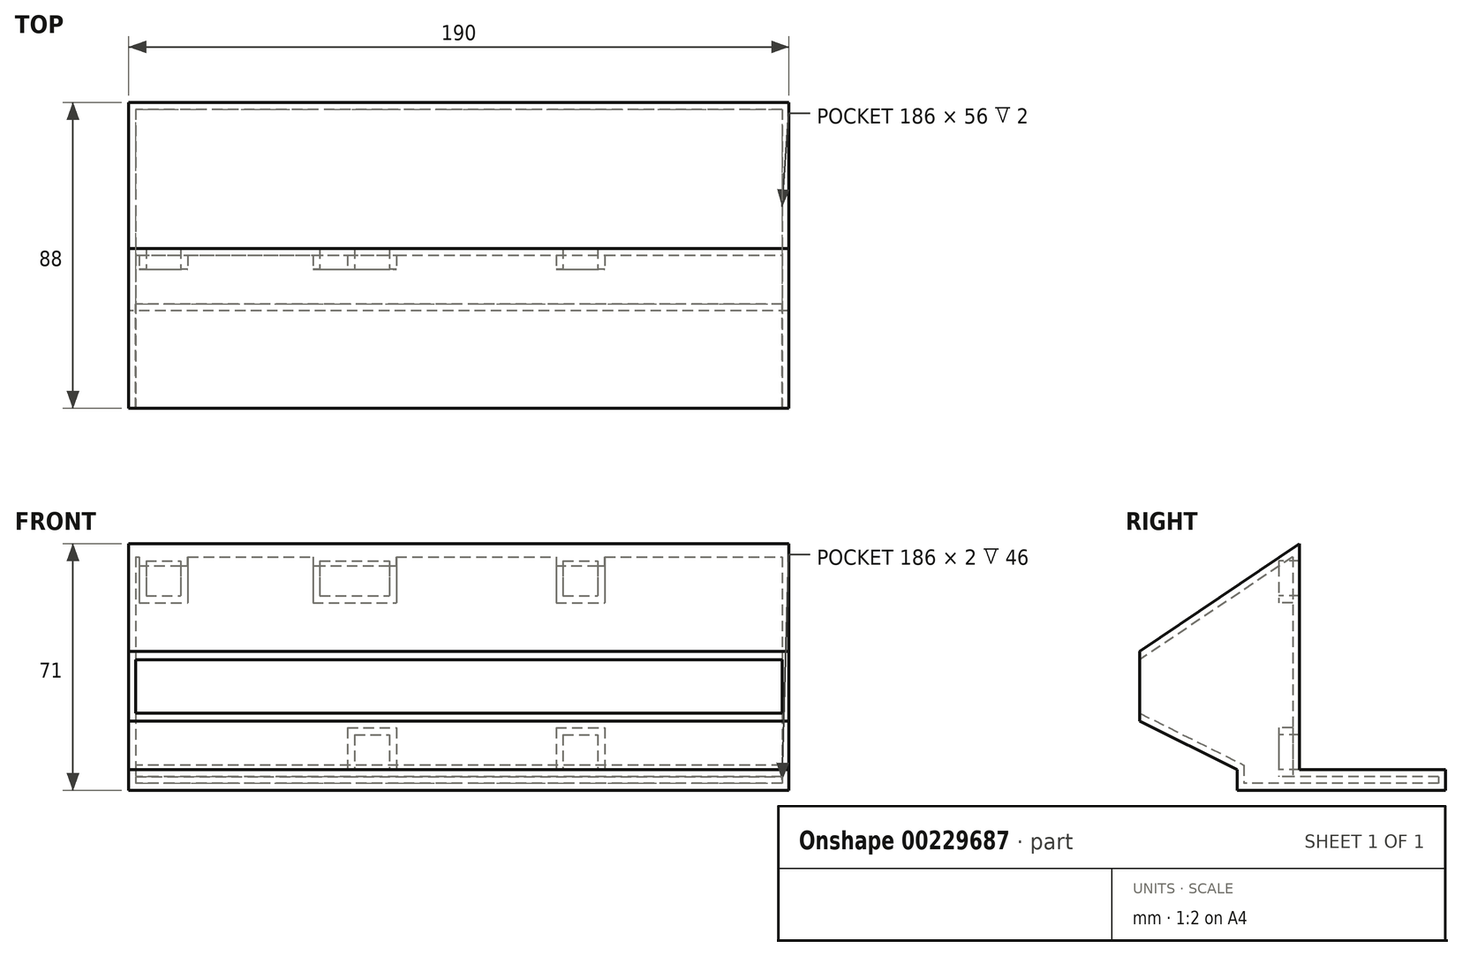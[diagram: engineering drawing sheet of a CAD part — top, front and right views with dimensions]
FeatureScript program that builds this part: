
annotation { "Feature Type Name" : "Feature", "Feature Type Description" : "" }
export const myFeature = defineFeature(function(context is Context, id is Id, definition is map)
    precondition{}
    {
        {
            var Q0;
            Q0=qCreatedBy(makeId("Top.planeOp"),FACE);
            var sketch = newSketch(context, id + "F0", { "sketchPlane" : qUnion([Q0])});
            skLineSegment(sketch, "E0.bottom", {"start": v(95, 30) * mm, "end": v(-95, 30) * mm});
            skLineSegment(sketch, "E0.top", {"start": v(95, -30) * mm, "end": v(-95, -30) * mm});
            skLineSegment(sketch, "E0.left", {"start": v(95, 30) * mm, "end": v(95, -30) * mm});
            skLineSegment(sketch, "E0.right", {"start": v(-95, 30) * mm, "end": v(-95, -30) * mm});
            skPoint(sketch, "E0.middle", {"position": v(0, 0) * mm});
            skSolve(sketch);
        }
        {
            var Q0;
            Q0=makeQuery(id+"F0.imprint","IMPRINT",FACE,{"disambiguationData":[TD([[makeQuery(id+"F0.imprint","IMPRINT",EDGE,{"derivedFrom":sQuery(id+"F0.wireOp",EDGE,"E0.bottom")}),1.0]])]});
            extrude(context, id + "F1", {"entities" : qUnion([Q0]), "depth" : 6 * mm});
        }
        {
            var Q0;
            Q0=makeQuery(id+"F1.opExtrude","CAP_FACE",FACE,{"disambiguationData":[OSD([sQuery(id+"F0.wireOp",EDGE,"E0.bottom"),sQuery(id+"F0.wireOp",EDGE,"E0.top"),sQuery(id+"F0.wireOp",EDGE,"E0.left"),sQuery(id+"F0.wireOp",EDGE,"E0.right")])],"isStart":false});
            var sketch = newSketch(context, id + "F2", { "sketchPlane" : qUnion([Q0])});
            skLineSegment(sketch, "E1.bottom", {"start": v(-95, -12) * mm, "end": v(95, -12) * mm});
            skLineSegment(sketch, "E1.top", {"start": v(-95, -18) * mm, "end": v(95, -18) * mm});
            skLineSegment(sketch, "E1.left", {"start": v(-95, -12) * mm, "end": v(-95, -18) * mm});
            skLineSegment(sketch, "E1.right", {"start": v(95, -12) * mm, "end": v(95, -18) * mm});
            skSolve(sketch);
        }
        {
            var Q0;
            Q0=makeQuery(id+"F2.imprint","IMPRINT",FACE,{"disambiguationData":[TD([[makeQuery(id+"F2.imprint","IMPRINT",EDGE,{"derivedFrom":sQuery(id+"F2.wireOp",EDGE,"E1.bottom")}),-1.0]])]});
            extrude(context, id + "F3", {"entities" : qUnion([Q0]), "operationType" : NewBodyOperationType.ADD, "depth" : 65 * mm});
        }
        {
            var Q0;
            Q0=makeQuery(id+"F3.opExtrude","SWEPT_FACE",FACE,{"disambiguationData":[OSD([sQuery(id+"F2.wireOp",EDGE,"E1.top")])]});
            var sketch = newSketch(context, id + "F4", { "sketchPlane" : qUnion([Q0])});
            skLineSegment(sketch, "E2.bottom", {"start": v(-90, 66) * mm, "end": v(-30, 66) * mm});
            skLineSegment(sketch, "E2.top", {"start": v(-90, 6) * mm, "end": v(-30, 6) * mm});
            skLineSegment(sketch, "E2.left", {"start": v(-90, 66) * mm, "end": v(-90, 6) * mm});
            skLineSegment(sketch, "E2.right", {"start": v(-30, 66) * mm, "end": v(-30, 6) * mm});
            skLineSegment(sketch, "E3.MirrorCS", {"start": v(30, 66) * mm, "end": v(-30, 66) * mm});
            skLineSegment(sketch, "E4.MirrorCS", {"start": v(30, 66) * mm, "end": v(30, 6) * mm});
            skLineSegment(sketch, "E5.MirrorCS", {"start": v(30, 6) * mm, "end": v(-30, 6) * mm});
            skLineSegment(sketch, "E6.MirrorCS", {"start": v(30, 66) * mm, "end": v(90, 66) * mm});
            skLineSegment(sketch, "E7.MirrorCS", {"start": v(90, 66) * mm, "end": v(90, 6) * mm});
            skLineSegment(sketch, "E8.MirrorCS", {"start": v(30, 6) * mm, "end": v(90, 6) * mm});
            skLineSegment(sketch, "E9.bottom", {"start": v(-90, 66) * mm, "end": v(-80, 66) * mm});
            skLineSegment(sketch, "E9.top", {"start": v(-90, 56) * mm, "end": v(-80, 56) * mm});
            skLineSegment(sketch, "E9.left", {"start": v(-90, 66) * mm, "end": v(-90, 56) * mm});
            skLineSegment(sketch, "E9.right", {"start": v(-80, 66) * mm, "end": v(-80, 56) * mm});
            skLineSegment(sketch, "E10.bottom", {"start": v(-90, 16) * mm, "end": v(-80, 16) * mm});
            skLineSegment(sketch, "E10.top", {"start": v(-90, 6) * mm, "end": v(-80, 6) * mm});
            skLineSegment(sketch, "E10.left", {"start": v(-90, 16) * mm, "end": v(-90, 6) * mm});
            skLineSegment(sketch, "E10.right", {"start": v(-80, 16) * mm, "end": v(-80, 6) * mm});
            skLineSegment(sketch, "E11.bottom", {"start": v(-40, 66) * mm, "end": v(-30, 66) * mm});
            skLineSegment(sketch, "E11.top", {"start": v(-40, 56) * mm, "end": v(-30, 56) * mm});
            skLineSegment(sketch, "E11.left", {"start": v(-40, 66) * mm, "end": v(-40, 56) * mm});
            skLineSegment(sketch, "E11.right", {"start": v(-30, 66) * mm, "end": v(-30, 56) * mm});
            skLineSegment(sketch, "E12.bottom", {"start": v(-40, 16) * mm, "end": v(-30, 16) * mm});
            skLineSegment(sketch, "E12.top", {"start": v(-40, 6) * mm, "end": v(-30, 6) * mm});
            skLineSegment(sketch, "E12.left", {"start": v(-40, 16) * mm, "end": v(-40, 6) * mm});
            skLineSegment(sketch, "E12.right", {"start": v(-30, 16) * mm, "end": v(-30, 6) * mm});
            skLineSegment(sketch, "E13.bottom", {"start": v(-30, 66) * mm, "end": v(-20, 66) * mm});
            skLineSegment(sketch, "E13.top", {"start": v(-30, 56) * mm, "end": v(-20, 56) * mm});
            skLineSegment(sketch, "E13.right", {"start": v(-20, 66) * mm, "end": v(-20, 56) * mm});
            skLineSegment(sketch, "E14.bottom", {"start": v(-30, 16) * mm, "end": v(-20, 16) * mm});
            skLineSegment(sketch, "E14.top", {"start": v(-30, 6) * mm, "end": v(-20, 6) * mm});
            skLineSegment(sketch, "E14.right", {"start": v(-20, 16) * mm, "end": v(-20, 6) * mm});
            skLineSegment(sketch, "E15.bottom", {"start": v(20, 16) * mm, "end": v(30, 16) * mm});
            skLineSegment(sketch, "E15.top", {"start": v(20, 6) * mm, "end": v(30, 6) * mm});
            skLineSegment(sketch, "E15.left", {"start": v(20, 16) * mm, "end": v(20, 6) * mm});
            skLineSegment(sketch, "E15.right", {"start": v(30, 16) * mm, "end": v(30, 6) * mm});
            skLineSegment(sketch, "E16.bottom", {"start": v(20, 66) * mm, "end": v(30, 66) * mm});
            skLineSegment(sketch, "E16.top", {"start": v(20, 56) * mm, "end": v(30, 56) * mm});
            skLineSegment(sketch, "E16.left", {"start": v(20, 66) * mm, "end": v(20, 56) * mm});
            skLineSegment(sketch, "E16.right", {"start": v(30, 66) * mm, "end": v(30, 56) * mm});
            skLineSegment(sketch, "E17.bottom", {"start": v(30, 66) * mm, "end": v(40, 66) * mm});
            skLineSegment(sketch, "E17.top", {"start": v(30, 56) * mm, "end": v(40, 56) * mm});
            skLineSegment(sketch, "E17.right", {"start": v(40, 66) * mm, "end": v(40, 56) * mm});
            skLineSegment(sketch, "E18.bottom", {"start": v(80, 66) * mm, "end": v(90, 66) * mm});
            skLineSegment(sketch, "E18.top", {"start": v(80, 56) * mm, "end": v(90, 56) * mm});
            skLineSegment(sketch, "E18.left", {"start": v(80, 66) * mm, "end": v(80, 56) * mm});
            skLineSegment(sketch, "E18.right", {"start": v(90, 66) * mm, "end": v(90, 56) * mm});
            skLineSegment(sketch, "E19.bottom", {"start": v(80, 16) * mm, "end": v(90, 16) * mm});
            skLineSegment(sketch, "E19.top", {"start": v(80, 6) * mm, "end": v(90, 6) * mm});
            skLineSegment(sketch, "E19.left", {"start": v(80, 16) * mm, "end": v(80, 6) * mm});
            skLineSegment(sketch, "E19.right", {"start": v(90, 16) * mm, "end": v(90, 6) * mm});
            skLineSegment(sketch, "E20.bottom", {"start": v(30, 16) * mm, "end": v(40, 16) * mm});
            skLineSegment(sketch, "E20.top", {"start": v(30, 6) * mm, "end": v(40, 6) * mm});
            skLineSegment(sketch, "E20.right", {"start": v(40, 16) * mm, "end": v(40, 6) * mm});
            skSolve(sketch);
        }
        {
            var Q0;
            Q0=makeQuery(id+"F4.imprint","IMPRINT",FACE,{"disambiguationData":[TD([[makeQuery(id+"F4.imprint","IMPRINT",EDGE,{"derivedFrom":sQuery(id+"F4.wireOp",EDGE,"E2.bottom")}),-1.0]])]});
            var Q1;
            Q1=makeQuery(id+"F4.imprint","IMPRINT",FACE,{"disambiguationData":[TD([[makeQuery(id+"F4.imprint","IMPRINT",EDGE,{"derivedFrom":sQuery(id+"F4.wireOp",EDGE,"E2.right")}),1.0]])]});
            var Q2;
            Q2=makeQuery(id+"F4.imprint","IMPRINT",FACE,{"disambiguationData":[TD([[makeQuery(id+"F4.imprint","IMPRINT",EDGE,{"derivedFrom":sQuery(id+"F4.wireOp",EDGE,"E4.MirrorCS")}),1.0]])]});
            extrude(context, id + "F5", {"entities" : qUnion([Q0, Q1, Q2]), "operationType" : NewBodyOperationType.REMOVE, "oppositeDirection" : true, "depth" : 6 * mm});
        }
        {
            var Q0;
            {var subQ2=sQuery(id+"F2.wireOp",EDGE,"E1.top");var subQ4=sQuery(id+"F0.wireOp",EDGE,"E0.left");Q0=makeQuery(id+"F5.boolean.opBoolean","SPLIT",FACE,{"disambiguationData":[TD([makeQuery(id+"F1.opExtrude","SWEPT_FACE",FACE,{"disambiguationData":[OSD([subQ4])]})])],"derivedFrom":makeQuery(id+"F3.opExtrude","SWEPT_FACE",FACE,{"disambiguationData":[OSD([subQ2])]})});}
            var sketch = newSketch(context, id + "F6", { "sketchPlane" : qUnion([Q0])});
            skLineSegment(sketch, "E21.bottom", {"start": v(-95, 71) * mm, "end": v(95, 71) * mm});
            skLineSegment(sketch, "E21.top", {"start": v(-95, 6) * mm, "end": v(95, 6) * mm});
            skLineSegment(sketch, "E21.left", {"start": v(-95, 71) * mm, "end": v(-95, 6) * mm});
            skLineSegment(sketch, "E21.right", {"start": v(95, 71) * mm, "end": v(95, 6) * mm});
            skSolve(sketch);
        }
        {
            var Q0;
            Q0 = qSketchRegion(id + "F6", true);
            extrude(context, id + "F7", {"entities" : qUnion([Q0]), "operationType" : NewBodyOperationType.ADD, "depth" : 40 * mm});
        }
        {
            var Q0;
            Q0=makeQuery(id+"F7.boolean.opBoolean","MERGE",FACE,{"derivedFrom":[makeQuery(id+"F3.boolean.opBoolean","MERGE",FACE,{"derivedFrom":[makeQuery(id+"F1.opExtrude","SWEPT_FACE",FACE,{"disambiguationData":[OSD([sQuery(id+"F0.wireOp",EDGE,"E0.right")])]}),makeQuery(id+"F3.opExtrude","SWEPT_FACE",FACE,{"disambiguationData":[OSD([sQuery(id+"F2.wireOp",EDGE,"E1.left")])]})]}),makeQuery(id+"F7.opExtrude","SWEPT_FACE",FACE,{"disambiguationData":[OSD([sQuery(id+"F6.wireOp",EDGE,"E21.left")])]})]});
            var sketch = newSketch(context, id + "F8", { "sketchPlane" : qUnion([Q0])});
            skLineSegment(sketch, "E22", {"start": v(58, 20) * mm, "end": v(30, 6) * mm});
            skLineSegment(sketch, "E23", {"start": v(12, 71) * mm, "end": v(58, 40) * mm});
            skSolve(sketch);
        }
        {
            var Q0;
            {var subQ0=sQuery(id+"F8.wireOp",EDGE,"E22");Q0=makeQuery(id+"F8.imprint","IMPRINT",FACE,{"disambiguationData":[TD([[makeQuery(id+"F8.imprint","IMPRINT",EDGE,{"derivedFrom":subQ0}),1.0]])]});}
            var Q1;
            {var subQ0=sQuery(id+"F8.wireOp",EDGE,"E23");Q1=makeQuery(id+"F8.imprint","IMPRINT",FACE,{"disambiguationData":[TD([[makeQuery(id+"F8.imprint","IMPRINT",EDGE,{"derivedFrom":subQ0}),1.0]])]});}
            extrude(context, id + "F9", {"entities" : qUnion([Q0, Q1]), "operationType" : NewBodyOperationType.REMOVE, "endBound" : BoundingType.UP_TO_NEXT, "oppositeDirection" : true, "depth" : 25 * mm});
        }
        {
            var Q0;
            Q0=makeQuery(id+"F7.opExtrude","CAP_FACE",FACE,{"disambiguationData":[OSD([sQuery(id+"F6.wireOp",EDGE,"E21.bottom"),sQuery(id+"F6.wireOp",EDGE,"E21.top"),sQuery(id+"F6.wireOp",EDGE,"E21.left"),sQuery(id+"F6.wireOp",EDGE,"E21.right")])],"isStart":true});
            var Q1;
            Q1=makeQuery(id+"F7.opExtrude","CAP_FACE",FACE,{"disambiguationData":[OSD([sQuery(id+"F6.wireOp",EDGE,"E21.bottom"),sQuery(id+"F6.wireOp",EDGE,"E21.top"),sQuery(id+"F6.wireOp",EDGE,"E21.left"),sQuery(id+"F6.wireOp",EDGE,"E21.right")])],"isStart":false});
            var Q2;
            Q2=makeQuery(id+"F1.opExtrude","SWEPT_BODY",BODY,{"disambiguationData":[OSD([sQuery(id+"F0.wireOp",EDGE,"E0.bottom"),sQuery(id+"F0.wireOp",EDGE,"E0.top"),sQuery(id+"F0.wireOp",EDGE,"E0.left"),sQuery(id+"F0.wireOp",EDGE,"E0.right")])]});
            shell(context, id + "F10", {"entities" : qUnion([Q0, Q1]), "parts" : qUnion([Q2]), "thickness" : 2 * mm});
        }
    });
